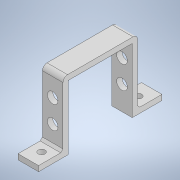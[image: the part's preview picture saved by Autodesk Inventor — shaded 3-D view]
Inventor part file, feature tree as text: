
AUTODESK INVENTOR PART (.ipt)
format: ipt  version: 2021 (Build 250183000, 183)  size: 155,648 bytes
history: native  units: mm
features: extrude x3, sketch x3, fillet x1, chamfer x1, pattern_linear x1
ambient origin geometry x8: Origin, YZ Plane, XZ Plane, XY Plane, X Axis, Y Axis, Z Axis, Center Point
bodies: Solid1 (feature_tree)
feature tree (9):
  extrude  "Extrusion1"  Depth=42.0mm
  extrude  "Extrusion3"  Depth=3.5mm
  fillet  "Fillet1"  Radius=13.5mm
  chamfer  "Chamfer1"  Distance=16.0mm
  extrude  "Extrusion5"  Depth=3.0mm
  pattern_linear  "Rectangular Pattern2"  Spacing1=4.5mm  [1 undecoded]
  sketch  "Sketch1"  dims[d3=42.2mm d4=42.0mm]
  sketch  "Sketch3"  dims[d5=3.5mm d7=3.5mm d9=13.5mm d10=0.0mm]
  sketch  "Sketch5"  dims[d19=16.0mm d20=16.0mm d21=4.5mm d22=4.5mm d23=6.75mm d24=6.75mm d25=8.75mm d26=8.75mm d27=0.0mm d28=0.0mm d29=3.0mm d30=1.5mm d31=2.0mm d32=45.0deg d44=7.0mm d45=15.0mm d46=0.0mm d47=0.0mm d48=20.0mm d50=15.0mm d51=6.75mm]
note: 1 required parameter value undecoded (feature->parameter linkage not recoverable at this tier; creation-order binding heuristic only, values carry confidence <= 0.55)
